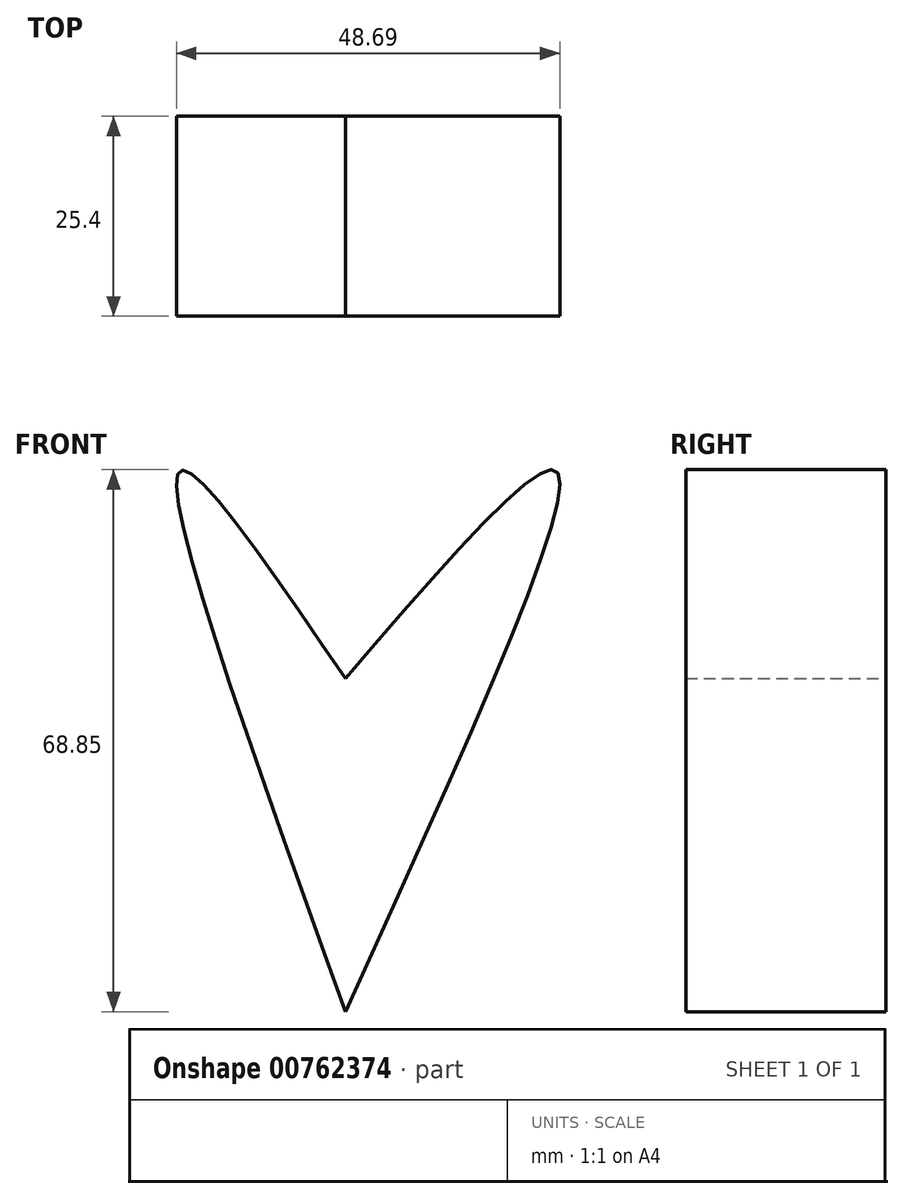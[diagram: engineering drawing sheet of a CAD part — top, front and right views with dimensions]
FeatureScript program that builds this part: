
annotation { "Feature Type Name" : "Feature", "Feature Type Description" : "" }
export const myFeature = defineFeature(function(context is Context, id is Id, definition is map)
    precondition{}
    {
        {
            var Q0;
            Q0=qCreatedBy(makeId("Front.planeOp"),FACE);
            var sketch = newSketch(context, id + "F0", { "sketchPlane" : qUnion([Q0])});
            skFitSpline(sketch, "E0", {"points": [v(0, 0) * mm, v(26.72, 26.42) * mm, v(0, -42.3) * mm], "startDerivative": vector(87.05, 101.15) * mm, "endDerivative": vector(-77.87, -170.62) * mm});
            skFitSpline(sketch, "E1", {"points": [v(0, 0) * mm, v(-20.92, 26.42) * mm, v(0, -42.3) * mm], "startDerivative": vector(-69.08, 101.72) * mm, "endDerivative": vector(60.98, -169.41) * mm});
            skSolve(sketch);
        }
        {
            var Q0;
            Q0=makeQuery(id+"F0.imprint","IMPRINT",FACE,{"disambiguationData":[TD([[makeQuery(id+"F0.imprint","IMPRINT",EDGE,{"derivedFrom":sQuery(id+"F0.wireOp",EDGE,"E0")}),-1.0]])]});
            extrude(context, id + "F1", {"entities" : qUnion([Q0]), "depth" : 25.4 * mm, "offsetDistance" : 25.4 * mm});
        }
    });
